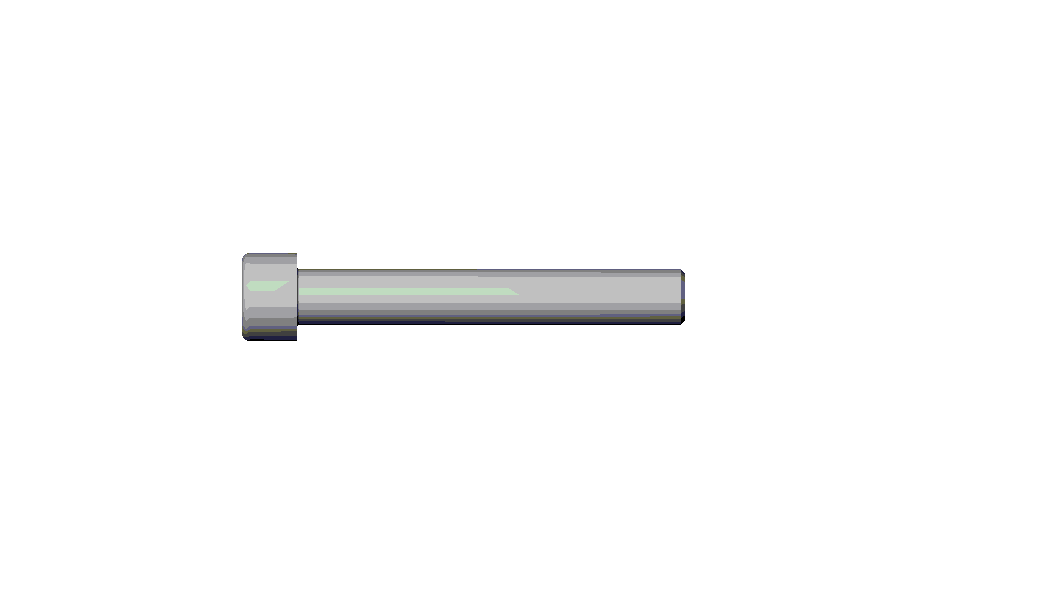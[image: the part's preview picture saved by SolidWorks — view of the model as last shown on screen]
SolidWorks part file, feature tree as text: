
SOLIDWORKS PART (.sldprt)
format: sldprt  version: not decoded by parser v0  size: 236,544 bytes
history: native  units: mm
features: sketch x4, plane x3, fillet x2, cut_revolve x2, material x1, revolve x1, thread x1, cut_extrude x1, pattern_linear x1 (+8 scaffold rows collapsed)
feature tree (24):
  scaffold x8  (default folders/planes/origin — collapsed)
  material  "Matériau <non spécifié>"
  plane  "Plane1"
  plane  "Plane2"
  plane  "Plane3"
  sketch  "BodySke"  dims[c1.Head_fillet_rad=1.016mm c1.Head_top_radius=2.54mm c1.D1=19.05mm c1.Diameter=25.4mm c1.D3=50.8mm c1.D4=22.225mm c2.D4=45.0deg c2.D5=22.225mm c2.Head_ht=10.0mm c2.Length=70.0mm c2.D8=9.525mm c3.D8=45.0deg c3.D1=9.525mm c4.D8=9.525mm c5.D8=45.0deg c5.D1=73.025mm c6.D1=45.0deg c7.D1=9.525mm c8.D1=45.0deg c8.D4=22.225mm c9.D4=45.0deg c9.Thread_min=12.7mm c10.D4=9.525mm c10.Body_ch_ang=45.0deg c10.D8=22.225mm c11.D8=45.0deg c11.D5=22.225mm c12.D5=45.0deg c13.D5=~4.490128mm c14.D5=45.0deg c14.Head_dia=50.8mm c15.D5=~8.980256mm c15.Head_ch_ang=45.0deg c15.Head_side_ht=22.86mm c15.D9=19.05mm c15.Diameter=10.0mm c15.Head_dia=38.1mm c15.Minor_dia=8.344mm c15.Advance=1.5mm c15.Thread_nom=60.0mm c15.Thread_lim=~74.083342mm c15.Thread_length=60.0mm c16.Head_dia=16.0mm]
  revolve  "Base-Revolve"  [1 undecoded]
  thread  "ThreadCosmetic"  Diameter=60mm Thread_length=60mm Thread_minor=8.344mm  [1 undecoded]
  fillet  "Fillet1"  Radius=0.4mm Head_dia=16mm
  fillet  "Fillet2"  Radius=1.5mm
  sketch  "Sketch2"  dims[c1.D1=4.0575mm c1.D2=25.4mm c2.D2=60.0deg c2.Wall_thickness=11.427mm c2.Depth=5.0mm]
  cut_revolve  "Hex-PreBroach"  Angle=360deg
  sketch  "Sketch3"  dims[c1.D1=4.0575mm c1.D2=4.0575mm c1.Hex_size=8.115mm c1.D4=~14.664697mm c2.D4=120.0deg]
  cut_extrude  "Hex"  Depth=5mm Key_eng=5mm
  sketch  "ThdSchSke"  dims[c1.Thread_minor=~1.03886mm c1.Diameter=~1.413535mm c1.Start=~0.988134mm c1.D4=~4.446753mm c1.Vee=60.0deg c2.Thread_minor=~1.03886mm c2.Start=~2.540025mm c2.D1=~0.108159mm c2.D2=~0.108159mm c3.D1=~0.216319mm c3.SideAngle=55.0deg c3.D2=~0.216319mm c3.VeeAngle=70.0deg c3.Thread_minor=8.344mm c3.Overcut=12.5mm c3.Diameter=10.0mm c3.D6=~8.326268mm c4.D1=~8.326268mm c5.D1=90.0deg c5.Start=54.0mm c6.Start=20.0mm]
  cut_revolve  "ThreadSchematic"  Angle=360deg
  pattern_linear  "ThdSchPat"  Count1=40 Count2=1 Spacing1=1.5mm Spacing2=50mm Num_threads=40 Advance=1.5mm ConfigurationName=0mm CopiedFlag=0 PartNumberID=0mm
decode coverage: 11 of 12 modeling features carry decoded parameters
note: ~ marks probable driven/reference dimensions
note: 2 parameter values undecoded
note: suppression state not decoded; provenance and decode notes live in map.json
